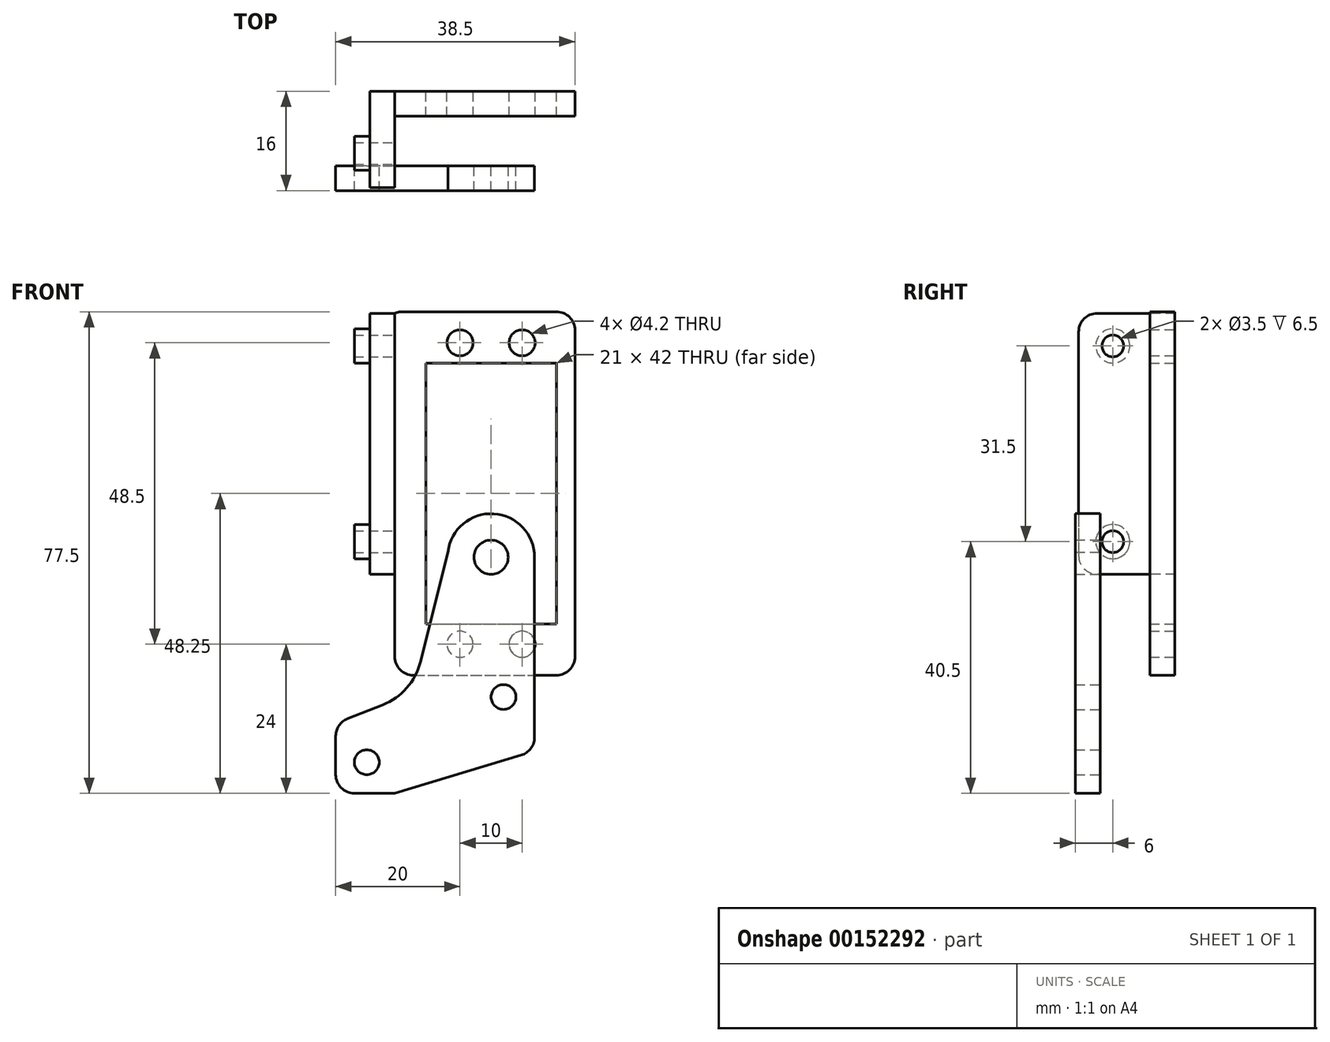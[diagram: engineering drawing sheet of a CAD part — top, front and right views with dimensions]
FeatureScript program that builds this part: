
annotation { "Feature Type Name" : "Feature", "Feature Type Description" : "" }
export const myFeature = defineFeature(function(context is Context, id is Id, definition is map)
    precondition{}
    {
        {
            var Q0;
            Q0=qCreatedBy(makeId("Right.planeOp"),FACE);
            var sketch = newSketch(context, id + "F0", { "sketchPlane" : qUnion([Q0])});
            skCircle(sketch, "E0", {"center": v(-10, 15.75) * mm, "radius": 1.75 * mm});
            skCircle(sketch, "E1", {"center": v(-10, -15.75) * mm, "radius": 1.75 * mm});
            skLineSegment(sketch, "E2", {"start": v(-10, 15.75) * mm, "end": v(-10, -15.75) * mm, "construction": true});
            skLineSegment(sketch, "E3", {"start": v(-10, 0) * mm, "end": v(0, 0) * mm, "construction": true});
            skLineSegment(sketch, "E4.bottom", {"start": v(0, 21) * mm, "end": v(-15.5, 21) * mm});
            skLineSegment(sketch, "E4.top", {"start": v(0, -21) * mm, "end": v(-15.5, -21) * mm});
            skLineSegment(sketch, "E4.left", {"start": v(0, 21) * mm, "end": v(0, -21) * mm});
            skLineSegment(sketch, "E4.right", {"start": v(-15.5, 21) * mm, "end": v(-15.5, -21) * mm});
            skSolve(sketch);
        }
        {
            var Q0;
            Q0 = qSketchRegion(id + "F0", true);
            extrude(context, id + "F1", {"entities" : qUnion([Q0]), "oppositeDirection" : true, "depth" : 4 * mm});
        }
        {
            var Q0;
            Q0=qCreatedBy(makeId("Front.planeOp"),FACE);
            var sketch = newSketch(context, id + "F2", { "sketchPlane" : qUnion([Q0])});
            skLineSegment(sketch, "E5.bottom", {"start": v(10.5, 16.25) * mm, "end": v(20.5, 16.25) * mm, "construction": true});
            skLineSegment(sketch, "E5.top", {"start": v(10.5, -32.25) * mm, "end": v(20.5, -32.25) * mm, "construction": true});
            skLineSegment(sketch, "E5.left", {"start": v(10.5, 16.25) * mm, "end": v(10.5, -32.25) * mm, "construction": true});
            skLineSegment(sketch, "E5.right", {"start": v(20.5, 16.25) * mm, "end": v(20.5, -32.25) * mm, "construction": true});
            skCircle(sketch, "E6", {"center": v(10.5, 16.25) * mm, "radius": 2.1 * mm});
            skCircle(sketch, "E7", {"center": v(20.5, 16.25) * mm, "radius": 2.1 * mm});
            skCircle(sketch, "E8", {"center": v(10.5, -32.25) * mm, "radius": 2.1 * mm});
            skCircle(sketch, "E9", {"center": v(20.5, -32.25) * mm, "radius": 2.1 * mm});
            skLineSegment(sketch, "E10.bottom", {"start": v(5, 13) * mm, "end": v(26, 13) * mm});
            skLineSegment(sketch, "E10.top", {"start": v(5, -29) * mm, "end": v(26, -29) * mm});
            skLineSegment(sketch, "E10.left", {"start": v(5, 13) * mm, "end": v(5, -29) * mm});
            skLineSegment(sketch, "E10.right", {"start": v(26, 13) * mm, "end": v(26, -29) * mm});
            skLineSegment(sketch, "E11", {"start": v(15.5, 16.25) * mm, "end": v(15.5, 13) * mm, "construction": true});
            skLineSegment(sketch, "E12", {"start": v(10.5, -8) * mm, "end": v(5, -8) * mm, "construction": true});
            skLineSegment(sketch, "E13.bottom", {"start": v(0, 21.25) * mm, "end": v(29, 21.25) * mm});
            skLineSegment(sketch, "E13.top", {"start": v(0, -37.25) * mm, "end": v(29, -37.25) * mm});
            skLineSegment(sketch, "E13.left", {"start": v(0, 21.25) * mm, "end": v(0, -37.25) * mm});
            skLineSegment(sketch, "E13.right", {"start": v(29, 21.25) * mm, "end": v(29, -37.25) * mm});
            skSolve(sketch);
        }
        {
            var Q0;
            Q0 = qSketchRegion(id + "F2", true);
            extrude(context, id + "F3", {"entities" : qUnion([Q0]), "operationType" : NewBodyOperationType.ADD, "depth" : 4 * mm});
        }
        {
            var Q0;
            Q0=makeQuery(id+"F1.opExtrude","SWEPT_EDGE",EDGE,{"disambiguationData":[OSD([sQuery(id+"F0.wireOp",EDGE,"E4.bottom"),sQuery(id+"F0.wireOp",EDGE,"E4.right")])]});
            var Q1;
            Q1=makeQuery(id+"F1.opExtrude","SWEPT_EDGE",EDGE,{"disambiguationData":[OSD([sQuery(id+"F0.wireOp",EDGE,"E4.top"),sQuery(id+"F0.wireOp",EDGE,"E4.right")])]});
            var Q2;
            Q2=makeQuery(id+"F3.opExtrude","SWEPT_EDGE",EDGE,{"disambiguationData":[OSD([sQuery(id+"F2.wireOp",EDGE,"E13.bottom"),sQuery(id+"F2.wireOp",EDGE,"E13.left")])]});
            var Q3;
            Q3=makeQuery(id+"F3.opExtrude","SWEPT_EDGE",EDGE,{"disambiguationData":[OSD([sQuery(id+"F2.wireOp",EDGE,"E13.bottom"),sQuery(id+"F2.wireOp",EDGE,"E13.right")])]});
            var Q4;
            Q4=makeQuery(id+"F3.opExtrude","SWEPT_EDGE",EDGE,{"disambiguationData":[OSD([sQuery(id+"F2.wireOp",EDGE,"E13.top"),sQuery(id+"F2.wireOp",EDGE,"E13.left")])]});
            var Q5;
            Q5=makeQuery(id+"F3.opExtrude","SWEPT_EDGE",EDGE,{"disambiguationData":[OSD([sQuery(id+"F2.wireOp",EDGE,"E13.top"),sQuery(id+"F2.wireOp",EDGE,"E13.right")])]});
            fillet(context, id + "F4", {"entities" : qUnion([Q0, Q1, Q2, Q3, Q4, Q5]), "radius" : 3 * mm, "tangentPropagation" : true, "allowEdgeOverflow" : false});
        }
        {
            var Q0;
            Q0=qCreatedBy(makeId("Front.planeOp"),FACE);
            cPlane(context, id + "F5", {"entities" : qUnion([Q0]), "cplaneType" : CPlaneType.OFFSET, "offset" : 12 * mm, "width" : 150 * mm, "height" : 150 * mm});
        }
        {
            var Q0;
            Q0=qCreatedBy(id+"F5.planeOp",FACE);
            var sketch = newSketch(context, id + "F6", { "sketchPlane" : qUnion([Q0])});
            skCircle(sketch, "E14", {"center": v(15.5, -18.25) * mm, "radius": 2.75 * mm});
            skLineSegment(sketch, "E15", {"start": v(15.5, -18.25) * mm, "end": v(15.5, -32.25) * mm, "construction": true});
            skCircle(sketch, "E16", {"center": v(15.5, -60.75) * mm, "radius": 2.5 * mm, "construction": true});
            skCircle(sketch, "E17", {"center": v(17.5, -40.75) * mm, "radius": 2 * mm});
            skCircle(sketch, "E18", {"center": v(-4.5, -51.25) * mm, "radius": 2 * mm});
            skLineSegment(sketch, "E19", {"start": v(15.5, -18.25) * mm, "end": v(15.5, -60.75) * mm, "construction": true});
            skSolve(sketch);
        }
        {
            var Q0;
            Q0=qCreatedBy(id+"F5.planeOp",FACE);
            var sketch = newSketch(context, id + "F7", { "sketchPlane" : qUnion([Q0])});
            skLineSegment(sketch, "E20", {"start": v(22.5, -18.25) * mm, "end": v(22.5, -49.46) * mm});
            skLineSegment(sketch, "E21", {"start": v(-9.5, -56.25) * mm, "end": v(-9.5, -45) * mm});
            skLineSegment(sketch, "E22", {"start": v(-9.5, -45) * mm, "end": v(2.86, -40.14) * mm});
            skLineSegment(sketch, "E23", {"start": v(2.86, -40.14) * mm, "end": v(8.55, -17.41) * mm});
            skCircle(sketch, "E24", {"center": v(15.5, -18.25) * mm, "radius": 7 * mm});
            skLineSegment(sketch, "E25", {"start": v(22.5, -49.46) * mm, "end": v(0, -56.25) * mm});
            skLineSegment(sketch, "E26", {"start": v(0, -56.25) * mm, "end": v(-9.5, -56.25) * mm});
            skSolve(sketch);
        }
        {
            var Q0;
            {var subQ1=sQuery(id+"F7.wireOp",EDGE,"E20");Q0=makeQuery(id+"F7.imprint","IMPRINT",FACE,{"disambiguationData":[TD([[makeQuery(id+"F7.imprint","IMPRINT",EDGE,{"derivedFrom":subQ1}),-1.0]])]});}
            var Q1;
            {var subQ0=sQuery(id+"F7.wireOp",EDGE,"E24");var subQ1=makeQuery(id+"F7.imprint","INTERSECT",VERTEX,{"derivedFrom":[sQuery(id+"F7.wireOp",EDGE,"E20"),subQ0]});Q1=makeQuery(id+"F7.imprint","IMPRINT",FACE,{"disambiguationData":[TD([[makeQuery(id+"F7.imprint","IMPRINT",EDGE,{"disambiguationData":[TD([[subQ1,-1.0]])],"derivedFrom":subQ0}),1.0]])]});}
            extrude(context, id + "F8", {"entities" : qUnion([Q0, Q1]), "depth" : 4 * mm});
        }
        {
            var Q0;
            Q0 = qSketchRegion(id + "F6", true);
            extrude(context, id + "F9", {"entities" : qUnion([Q0]), "operationType" : NewBodyOperationType.REMOVE, "depth" : 25 * mm});
        }
        {
            var Q0;
            Q0=makeQuery(id+"F8.opExtrude","SWEPT_EDGE",EDGE,{"disambiguationData":[OSD([sQuery(id+"F7.wireOp",EDGE,"E21"),sQuery(id+"F7.wireOp",EDGE,"E22")])]});
            var Q1;
            Q1=makeQuery(id+"F8.opExtrude","SWEPT_EDGE",EDGE,{"disambiguationData":[OSD([sQuery(id+"F7.wireOp",EDGE,"E20"),sQuery(id+"F7.wireOp",EDGE,"e78LslJy-gSW1-Cbj8-qCXM-QcJlXIkdy4ha")])]});
            var Q2;
            Q2=makeQuery(id+"F8.opExtrude","SWEPT_EDGE",EDGE,{"disambiguationData":[OSD([sQuery(id+"F7.wireOp",EDGE,"e78LslJy-gSW1-Cbj8-qCXM-QcJlXIkdy4ha"),sQuery(id+"F7.wireOp",EDGE,"ZmI5YXVM-5TeL-KG2Z-oNVk-KKRN8MTRBtOJ")])]});
            var Q3;
            Q3=makeQuery(id+"F8.opExtrude","SWEPT_EDGE",EDGE,{"disambiguationData":[OSD([sQuery(id+"F7.wireOp",EDGE,"ZmI5YXVM-5TeL-KG2Z-oNVk-KKRN8MTRBtOJ"),sQuery(id+"F7.wireOp",EDGE,"E21")])]});
            fillet(context, id + "F10", {"entities" : qUnion([Q0, Q1, Q2, Q3]), "radius" : 3 * mm, "tangentPropagation" : true, "allowEdgeOverflow" : false});
        }
        {
            var Q0;
            Q0=makeQuery(id+"F8.opExtrude","SWEPT_EDGE",EDGE,{"disambiguationData":[OSD([sQuery(id+"F7.wireOp",EDGE,"E22"),sQuery(id+"F7.wireOp",EDGE,"E23")])]});
            fillet(context, id + "F11", {"entities" : qUnion([Q0]), "radius" : 10 * mm, "tangentPropagation" : true, "allowEdgeOverflow" : false});
        }
        {
            var Q0;
            Q0=makeQuery(id+"F1.opExtrude","CAP_FACE",FACE,{"disambiguationData":[OSD([sQuery(id+"F0.wireOp",EDGE,"E0"),sQuery(id+"F0.wireOp",EDGE,"E1"),sQuery(id+"F0.wireOp",EDGE,"E4.bottom"),sQuery(id+"F0.wireOp",EDGE,"E4.top"),sQuery(id+"F0.wireOp",EDGE,"E4.left"),sQuery(id+"F0.wireOp",EDGE,"E4.right")])],"isStart":false});
            var sketch = newSketch(context, id + "F12", { "sketchPlane" : qUnion([Q0])});
            skCircle(sketch, "E27", {"center": v(10, 15.75) * mm, "radius": 2.75 * mm});
            skCircle(sketch, "E28", {"center": v(10, -15.75) * mm, "radius": 2.75 * mm});
            skSolve(sketch);
        }
        {
            var Q0;
            Q0=makeQuery(id+"F12.imprint","IMPRINT",FACE,{"disambiguationData":[TD([[makeQuery(id+"F12.imprint","IMPRINT",EDGE,{"derivedFrom":sQuery(id+"F12.wireOp",EDGE,"E27")}),1.0]])]});
            var Q1;
            Q1=makeQuery(id+"F12.imprint","IMPRINT",FACE,{"disambiguationData":[TD([[makeQuery(id+"F12.imprint","IMPRINT",EDGE,{"derivedFrom":sQuery(id+"F12.wireOp",EDGE,"E28")}),1.0]])]});
            extrude(context, id + "F13", {"entities" : qUnion([Q0, Q1]), "operationType" : NewBodyOperationType.ADD, "depth" : 2.5 * mm});
        }
    });
